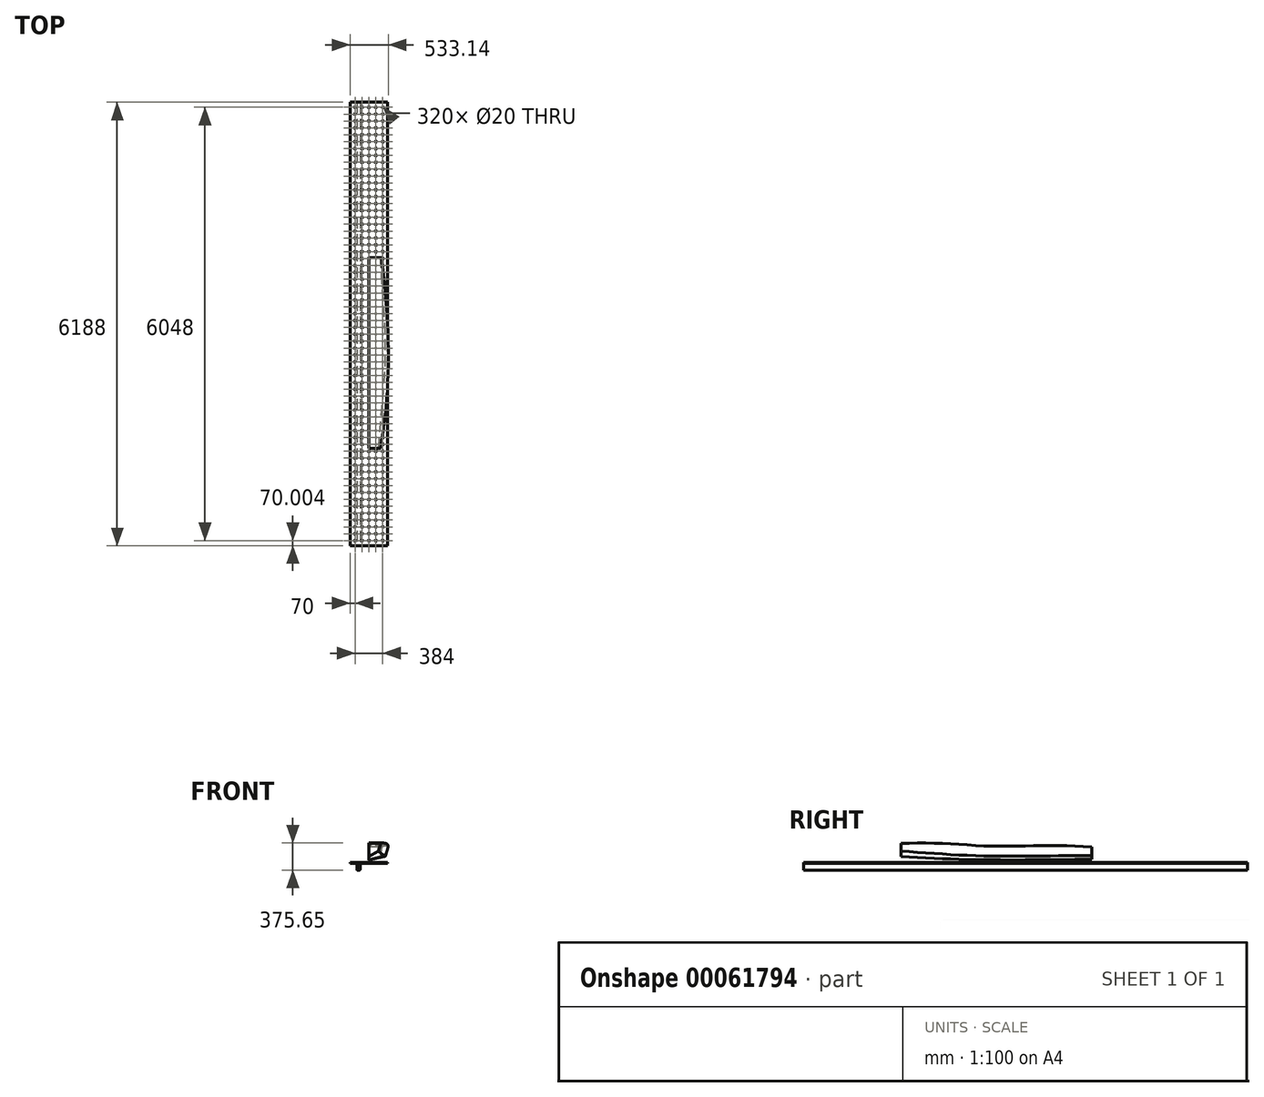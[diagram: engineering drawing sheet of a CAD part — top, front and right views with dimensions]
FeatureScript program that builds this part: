
annotation { "Feature Type Name" : "Feature", "Feature Type Description" : "" }
export const myFeature = defineFeature(function(context is Context, id is Id, definition is map)
    precondition{}
    {
        {
            var Q0;
            Q0=qCreatedBy(makeId("Right.planeOp"),FACE);
            var sketch = newSketch(context, id + "F0", { "sketchPlane" : qUnion([Q0])});
            skLineSegment(sketch, "E0.bottom", {"start": v(-75.52, -5.51) * mm, "end": v(6112.48, -5.51) * mm});
            skLineSegment(sketch, "E0.top", {"start": v(-75.52, 12.49) * mm, "end": v(6112.48, 12.49) * mm});
            skLineSegment(sketch, "E0.left", {"start": v(-75.52, -5.51) * mm, "end": v(-75.52, 12.49) * mm});
            skLineSegment(sketch, "E0.right", {"start": v(6112.48, -5.51) * mm, "end": v(6112.48, 12.49) * mm});
            skSolve(sketch);
        }
        {
            var Q0;
            Q0 = qSketchRegion(id + "F0", true);
            extrude(context, id + "F1", {"entities" : qUnion([Q0]), "endBound" : BoundingType.SYMMETRIC, "depth" : 524 * mm});
        }
        {
            var Q0;
            Q0=makeQuery(id+"F1.opExtrude","SWEPT_FACE",FACE,{"disambiguationData":[OSD([sQuery(id+"F0.wireOp",EDGE,"E0.top")])]});
            var sketch = newSketch(context, id + "F2", { "sketchPlane" : qUnion([Q0])});
            skCircle(sketch, "E1", {"center": v(0, -5.52) * mm, "radius": 10 * mm});
            skPoint(sketch, "E1.centerSnap0", {"position": v(0, -75.52) * mm});
            skCircle(sketch, "E2.0.1.0", {"center": v(0, 90.48) * mm, "radius": 10 * mm});
            skCircle(sketch, "E2.0.2.0", {"center": v(0, 186.48) * mm, "radius": 10 * mm});
            skCircle(sketch, "E2.0.3.0", {"center": v(0, 282.48) * mm, "radius": 10 * mm});
            skCircle(sketch, "E2.0.4.0", {"center": v(0, 378.48) * mm, "radius": 10 * mm});
            skCircle(sketch, "E2.0.5.0", {"center": v(0, 474.48) * mm, "radius": 10 * mm});
            skCircle(sketch, "E2.0.6.0", {"center": v(0, 570.48) * mm, "radius": 10 * mm});
            skCircle(sketch, "E2.0.7.0", {"center": v(0, 666.48) * mm, "radius": 10 * mm});
            skCircle(sketch, "E2.0.8.0", {"center": v(0, 762.48) * mm, "radius": 10 * mm});
            skCircle(sketch, "E2.0.9.0", {"center": v(0, 858.48) * mm, "radius": 10 * mm});
            skCircle(sketch, "E2.0.10.0", {"center": v(0, 954.48) * mm, "radius": 10 * mm});
            skCircle(sketch, "E2.0.11.0", {"center": v(0, 1050.48) * mm, "radius": 10 * mm});
            skCircle(sketch, "E2.0.12.0", {"center": v(0, 1146.48) * mm, "radius": 10 * mm});
            skCircle(sketch, "E2.0.13.0", {"center": v(0, 1242.48) * mm, "radius": 10 * mm});
            skCircle(sketch, "E2.0.14.0", {"center": v(0, 1338.48) * mm, "radius": 10 * mm});
            skCircle(sketch, "E2.0.15.0", {"center": v(0, 1434.48) * mm, "radius": 10 * mm});
            skCircle(sketch, "E2.0.16.0", {"center": v(0, 1530.48) * mm, "radius": 10 * mm});
            skCircle(sketch, "E2.0.17.0", {"center": v(0, 1626.48) * mm, "radius": 10 * mm});
            skCircle(sketch, "E2.0.18.0", {"center": v(0, 1722.48) * mm, "radius": 10 * mm});
            skCircle(sketch, "E2.0.19.0", {"center": v(0, 1818.48) * mm, "radius": 10 * mm});
            skCircle(sketch, "E2.0.20.0", {"center": v(0, 1914.48) * mm, "radius": 10 * mm});
            skCircle(sketch, "E2.0.21.0", {"center": v(0, 2010.48) * mm, "radius": 10 * mm});
            skCircle(sketch, "E2.0.22.0", {"center": v(0, 2106.48) * mm, "radius": 10 * mm});
            skCircle(sketch, "E2.0.23.0", {"center": v(0, 2202.48) * mm, "radius": 10 * mm});
            skCircle(sketch, "E2.0.24.0", {"center": v(0, 2298.48) * mm, "radius": 10 * mm});
            skCircle(sketch, "E2.0.25.0", {"center": v(0, 2394.48) * mm, "radius": 10 * mm});
            skCircle(sketch, "E2.0.26.0", {"center": v(0, 2490.48) * mm, "radius": 10 * mm});
            skCircle(sketch, "E2.0.27.0", {"center": v(0, 2586.48) * mm, "radius": 10 * mm});
            skCircle(sketch, "E2.0.28.0", {"center": v(0, 2682.48) * mm, "radius": 10 * mm});
            skCircle(sketch, "E2.0.29.0", {"center": v(0, 2778.48) * mm, "radius": 10 * mm});
            skCircle(sketch, "E2.0.30.0", {"center": v(0, 2874.48) * mm, "radius": 10 * mm});
            skCircle(sketch, "E2.0.31.0", {"center": v(0, 2970.48) * mm, "radius": 10 * mm});
            skCircle(sketch, "E2.0.32.0", {"center": v(0, 3066.48) * mm, "radius": 10 * mm});
            skCircle(sketch, "E2.0.33.0", {"center": v(0, 3162.48) * mm, "radius": 10 * mm});
            skCircle(sketch, "E2.0.34.0", {"center": v(0, 3258.48) * mm, "radius": 10 * mm});
            skCircle(sketch, "E2.0.35.0", {"center": v(0, 3354.48) * mm, "radius": 10 * mm});
            skCircle(sketch, "E2.0.36.0", {"center": v(0, 3450.48) * mm, "radius": 10 * mm});
            skCircle(sketch, "E2.0.37.0", {"center": v(0, 3546.48) * mm, "radius": 10 * mm});
            skCircle(sketch, "E2.0.38.0", {"center": v(0, 3642.48) * mm, "radius": 10 * mm});
            skCircle(sketch, "E2.0.39.0", {"center": v(0, 3738.48) * mm, "radius": 10 * mm});
            skCircle(sketch, "E2.0.40.0", {"center": v(0, 3834.48) * mm, "radius": 10 * mm});
            skCircle(sketch, "E2.0.41.0", {"center": v(0, 3930.48) * mm, "radius": 10 * mm});
            skCircle(sketch, "E2.0.42.0", {"center": v(0, 4026.48) * mm, "radius": 10 * mm});
            skCircle(sketch, "E2.0.43.0", {"center": v(0, 4122.48) * mm, "radius": 10 * mm});
            skCircle(sketch, "E2.0.44.0", {"center": v(0, 4218.48) * mm, "radius": 10 * mm});
            skCircle(sketch, "E2.0.45.0", {"center": v(0, 4314.48) * mm, "radius": 10 * mm});
            skCircle(sketch, "E2.0.46.0", {"center": v(0, 4410.48) * mm, "radius": 10 * mm});
            skCircle(sketch, "E2.0.47.0", {"center": v(0, 4506.48) * mm, "radius": 10 * mm});
            skCircle(sketch, "E2.0.48.0", {"center": v(0, 4602.48) * mm, "radius": 10 * mm});
            skCircle(sketch, "E2.0.49.0", {"center": v(0, 4698.48) * mm, "radius": 10 * mm});
            skCircle(sketch, "E2.1.0.0", {"center": v(96, -5.52) * mm, "radius": 10 * mm});
            skCircle(sketch, "E2.1.1.0", {"center": v(96, 90.48) * mm, "radius": 10 * mm});
            skCircle(sketch, "E2.1.2.0", {"center": v(96, 186.48) * mm, "radius": 10 * mm});
            skCircle(sketch, "E2.1.3.0", {"center": v(96, 282.48) * mm, "radius": 10 * mm});
            skCircle(sketch, "E2.1.4.0", {"center": v(96, 378.48) * mm, "radius": 10 * mm});
            skCircle(sketch, "E2.1.5.0", {"center": v(96, 474.48) * mm, "radius": 10 * mm});
            skCircle(sketch, "E2.1.6.0", {"center": v(96, 570.48) * mm, "radius": 10 * mm});
            skCircle(sketch, "E2.1.7.0", {"center": v(96, 666.48) * mm, "radius": 10 * mm});
            skCircle(sketch, "E2.1.8.0", {"center": v(96, 762.48) * mm, "radius": 10 * mm});
            skCircle(sketch, "E2.1.9.0", {"center": v(96, 858.48) * mm, "radius": 10 * mm});
            skCircle(sketch, "E2.1.10.0", {"center": v(96, 954.48) * mm, "radius": 10 * mm});
            skCircle(sketch, "E2.1.11.0", {"center": v(96, 1050.48) * mm, "radius": 10 * mm});
            skCircle(sketch, "E2.1.12.0", {"center": v(96, 1146.48) * mm, "radius": 10 * mm});
            skCircle(sketch, "E2.1.13.0", {"center": v(96, 1242.48) * mm, "radius": 10 * mm});
            skCircle(sketch, "E2.1.14.0", {"center": v(96, 1338.48) * mm, "radius": 10 * mm});
            skCircle(sketch, "E2.1.15.0", {"center": v(96, 1434.48) * mm, "radius": 10 * mm});
            skCircle(sketch, "E2.1.16.0", {"center": v(96, 1530.48) * mm, "radius": 10 * mm});
            skCircle(sketch, "E2.1.17.0", {"center": v(96, 1626.48) * mm, "radius": 10 * mm});
            skCircle(sketch, "E2.1.18.0", {"center": v(96, 1722.48) * mm, "radius": 10 * mm});
            skCircle(sketch, "E2.1.19.0", {"center": v(96, 1818.48) * mm, "radius": 10 * mm});
            skCircle(sketch, "E2.1.20.0", {"center": v(96, 1914.48) * mm, "radius": 10 * mm});
            skCircle(sketch, "E2.1.21.0", {"center": v(96, 2010.48) * mm, "radius": 10 * mm});
            skCircle(sketch, "E2.1.22.0", {"center": v(96, 2106.48) * mm, "radius": 10 * mm});
            skCircle(sketch, "E2.1.23.0", {"center": v(96, 2202.48) * mm, "radius": 10 * mm});
            skCircle(sketch, "E2.1.24.0", {"center": v(96, 2298.48) * mm, "radius": 10 * mm});
            skCircle(sketch, "E2.1.25.0", {"center": v(96, 2394.48) * mm, "radius": 10 * mm});
            skCircle(sketch, "E2.1.26.0", {"center": v(96, 2490.48) * mm, "radius": 10 * mm});
            skCircle(sketch, "E2.1.27.0", {"center": v(96, 2586.48) * mm, "radius": 10 * mm});
            skCircle(sketch, "E2.1.28.0", {"center": v(96, 2682.48) * mm, "radius": 10 * mm});
            skCircle(sketch, "E2.1.29.0", {"center": v(96, 2778.48) * mm, "radius": 10 * mm});
            skCircle(sketch, "E2.1.30.0", {"center": v(96, 2874.48) * mm, "radius": 10 * mm});
            skCircle(sketch, "E2.1.31.0", {"center": v(96, 2970.48) * mm, "radius": 10 * mm});
            skCircle(sketch, "E2.1.32.0", {"center": v(96, 3066.48) * mm, "radius": 10 * mm});
            skCircle(sketch, "E2.1.33.0", {"center": v(96, 3162.48) * mm, "radius": 10 * mm});
            skCircle(sketch, "E2.1.34.0", {"center": v(96, 3258.48) * mm, "radius": 10 * mm});
            skCircle(sketch, "E2.1.35.0", {"center": v(96, 3354.48) * mm, "radius": 10 * mm});
            skCircle(sketch, "E2.1.36.0", {"center": v(96, 3450.48) * mm, "radius": 10 * mm});
            skCircle(sketch, "E2.1.37.0", {"center": v(96, 3546.48) * mm, "radius": 10 * mm});
            skCircle(sketch, "E2.1.38.0", {"center": v(96, 3642.48) * mm, "radius": 10 * mm});
            skCircle(sketch, "E2.1.39.0", {"center": v(96, 3738.48) * mm, "radius": 10 * mm});
            skCircle(sketch, "E2.1.40.0", {"center": v(96, 3834.48) * mm, "radius": 10 * mm});
            skCircle(sketch, "E2.1.41.0", {"center": v(96, 3930.48) * mm, "radius": 10 * mm});
            skCircle(sketch, "E2.1.42.0", {"center": v(96, 4026.48) * mm, "radius": 10 * mm});
            skCircle(sketch, "E2.1.43.0", {"center": v(96, 4122.48) * mm, "radius": 10 * mm});
            skCircle(sketch, "E2.1.44.0", {"center": v(96, 4218.48) * mm, "radius": 10 * mm});
            skCircle(sketch, "E2.1.45.0", {"center": v(96, 4314.48) * mm, "radius": 10 * mm});
            skCircle(sketch, "E2.1.46.0", {"center": v(96, 4410.48) * mm, "radius": 10 * mm});
            skCircle(sketch, "E2.1.47.0", {"center": v(96, 4506.48) * mm, "radius": 10 * mm});
            skCircle(sketch, "E2.1.48.0", {"center": v(96, 4602.48) * mm, "radius": 10 * mm});
            skCircle(sketch, "E2.1.49.0", {"center": v(96, 4698.48) * mm, "radius": 10 * mm});
            skCircle(sketch, "E2.2.0.0", {"center": v(192, -5.52) * mm, "radius": 10 * mm});
            skCircle(sketch, "E2.2.1.0", {"center": v(192, 90.48) * mm, "radius": 10 * mm});
            skCircle(sketch, "E2.2.2.0", {"center": v(192, 186.48) * mm, "radius": 10 * mm});
            skCircle(sketch, "E2.2.3.0", {"center": v(192, 282.48) * mm, "radius": 10 * mm});
            skCircle(sketch, "E2.2.4.0", {"center": v(192, 378.48) * mm, "radius": 10 * mm});
            skCircle(sketch, "E2.2.5.0", {"center": v(192, 474.48) * mm, "radius": 10 * mm});
            skCircle(sketch, "E2.2.6.0", {"center": v(192, 570.48) * mm, "radius": 10 * mm});
            skCircle(sketch, "E2.2.7.0", {"center": v(192, 666.48) * mm, "radius": 10 * mm});
            skCircle(sketch, "E2.2.8.0", {"center": v(192, 762.48) * mm, "radius": 10 * mm});
            skCircle(sketch, "E2.2.9.0", {"center": v(192, 858.48) * mm, "radius": 10 * mm});
            skCircle(sketch, "E2.2.10.0", {"center": v(192, 954.48) * mm, "radius": 10 * mm});
            skCircle(sketch, "E2.2.11.0", {"center": v(192, 1050.48) * mm, "radius": 10 * mm});
            skCircle(sketch, "E2.2.12.0", {"center": v(192, 1146.48) * mm, "radius": 10 * mm});
            skCircle(sketch, "E2.2.13.0", {"center": v(192, 1242.48) * mm, "radius": 10 * mm});
            skCircle(sketch, "E2.2.14.0", {"center": v(192, 1338.48) * mm, "radius": 10 * mm});
            skCircle(sketch, "E2.2.15.0", {"center": v(192, 1434.48) * mm, "radius": 10 * mm});
            skCircle(sketch, "E2.2.16.0", {"center": v(192, 1530.48) * mm, "radius": 10 * mm});
            skCircle(sketch, "E2.2.17.0", {"center": v(192, 1626.48) * mm, "radius": 10 * mm});
            skCircle(sketch, "E2.2.18.0", {"center": v(192, 1722.48) * mm, "radius": 10 * mm});
            skCircle(sketch, "E2.2.19.0", {"center": v(192, 1818.48) * mm, "radius": 10 * mm});
            skCircle(sketch, "E2.2.20.0", {"center": v(192, 1914.48) * mm, "radius": 10 * mm});
            skCircle(sketch, "E2.2.21.0", {"center": v(192, 2010.48) * mm, "radius": 10 * mm});
            skCircle(sketch, "E2.2.22.0", {"center": v(192, 2106.48) * mm, "radius": 10 * mm});
            skCircle(sketch, "E2.2.23.0", {"center": v(192, 2202.48) * mm, "radius": 10 * mm});
            skCircle(sketch, "E2.2.24.0", {"center": v(192, 2298.48) * mm, "radius": 10 * mm});
            skCircle(sketch, "E2.2.25.0", {"center": v(192, 2394.48) * mm, "radius": 10 * mm});
            skCircle(sketch, "E2.2.26.0", {"center": v(192, 2490.48) * mm, "radius": 10 * mm});
            skCircle(sketch, "E2.2.27.0", {"center": v(192, 2586.48) * mm, "radius": 10 * mm});
            skCircle(sketch, "E2.2.28.0", {"center": v(192, 2682.48) * mm, "radius": 10 * mm});
            skCircle(sketch, "E2.2.29.0", {"center": v(192, 2778.48) * mm, "radius": 10 * mm});
            skCircle(sketch, "E2.2.30.0", {"center": v(192, 2874.48) * mm, "radius": 10 * mm});
            skCircle(sketch, "E2.2.31.0", {"center": v(192, 2970.48) * mm, "radius": 10 * mm});
            skCircle(sketch, "E2.2.32.0", {"center": v(192, 3066.48) * mm, "radius": 10 * mm});
            skCircle(sketch, "E2.2.33.0", {"center": v(192, 3162.48) * mm, "radius": 10 * mm});
            skCircle(sketch, "E2.2.34.0", {"center": v(192, 3258.48) * mm, "radius": 10 * mm});
            skCircle(sketch, "E2.2.35.0", {"center": v(192, 3354.48) * mm, "radius": 10 * mm});
            skCircle(sketch, "E2.2.36.0", {"center": v(192, 3450.48) * mm, "radius": 10 * mm});
            skCircle(sketch, "E2.2.37.0", {"center": v(192, 3546.48) * mm, "radius": 10 * mm});
            skCircle(sketch, "E2.2.38.0", {"center": v(192, 3642.48) * mm, "radius": 10 * mm});
            skCircle(sketch, "E2.2.39.0", {"center": v(192, 3738.48) * mm, "radius": 10 * mm});
            skCircle(sketch, "E2.2.40.0", {"center": v(192, 3834.48) * mm, "radius": 10 * mm});
            skCircle(sketch, "E2.2.41.0", {"center": v(192, 3930.48) * mm, "radius": 10 * mm});
            skCircle(sketch, "E2.2.42.0", {"center": v(192, 4026.48) * mm, "radius": 10 * mm});
            skCircle(sketch, "E2.2.43.0", {"center": v(192, 4122.48) * mm, "radius": 10 * mm});
            skCircle(sketch, "E2.2.44.0", {"center": v(192, 4218.48) * mm, "radius": 10 * mm});
            skCircle(sketch, "E2.2.45.0", {"center": v(192, 4314.48) * mm, "radius": 10 * mm});
            skCircle(sketch, "E2.2.46.0", {"center": v(192, 4410.48) * mm, "radius": 10 * mm});
            skCircle(sketch, "E2.2.47.0", {"center": v(192, 4506.48) * mm, "radius": 10 * mm});
            skCircle(sketch, "E2.2.48.0", {"center": v(192, 4602.48) * mm, "radius": 10 * mm});
            skCircle(sketch, "E2.2.49.0", {"center": v(192, 4698.48) * mm, "radius": 10 * mm});
            skLineSegment(sketch, "E2.direction1", {"start": v(0, -5.52) * mm, "end": v(96, -5.52) * mm, "construction": true});
            skLineSegment(sketch, "E2.direction2", {"start": v(0, -5.52) * mm, "end": v(0, 90.48) * mm, "construction": true});
            skCircle(sketch, "E3.0.0.50", {"center": v(0, 4794.48) * mm, "radius": 10 * mm});
            skCircle(sketch, "E3.0.0.51", {"center": v(0, 4890.48) * mm, "radius": 10 * mm});
            skCircle(sketch, "E3.0.0.52", {"center": v(0, 4986.48) * mm, "radius": 10 * mm});
            skCircle(sketch, "E3.0.0.53", {"center": v(0, 5082.48) * mm, "radius": 10 * mm});
            skCircle(sketch, "E3.0.0.54", {"center": v(0, 5178.48) * mm, "radius": 10 * mm});
            skCircle(sketch, "E3.0.0.55", {"center": v(0, 5274.48) * mm, "radius": 10 * mm});
            skCircle(sketch, "E3.0.0.56", {"center": v(0, 5370.48) * mm, "radius": 10 * mm});
            skCircle(sketch, "E3.0.0.57", {"center": v(0, 5466.48) * mm, "radius": 10 * mm});
            skCircle(sketch, "E3.0.0.58", {"center": v(0, 5562.48) * mm, "radius": 10 * mm});
            skCircle(sketch, "E3.0.0.59", {"center": v(0, 5658.48) * mm, "radius": 10 * mm});
            skCircle(sketch, "E3.0.0.60", {"center": v(0, 5754.48) * mm, "radius": 10 * mm});
            skCircle(sketch, "E3.0.0.61", {"center": v(0, 5850.48) * mm, "radius": 10 * mm});
            skCircle(sketch, "E3.0.0.62", {"center": v(0, 5946.48) * mm, "radius": 10 * mm});
            skCircle(sketch, "E3.0.0.63", {"center": v(0, 6042.48) * mm, "radius": 10 * mm});
            skCircle(sketch, "E3.0.1.50", {"center": v(96, 4794.48) * mm, "radius": 10 * mm});
            skCircle(sketch, "E3.0.1.51", {"center": v(96, 4890.48) * mm, "radius": 10 * mm});
            skCircle(sketch, "E3.0.1.52", {"center": v(96, 4986.48) * mm, "radius": 10 * mm});
            skCircle(sketch, "E3.0.1.53", {"center": v(96, 5082.48) * mm, "radius": 10 * mm});
            skCircle(sketch, "E3.0.1.54", {"center": v(96, 5178.48) * mm, "radius": 10 * mm});
            skCircle(sketch, "E3.0.1.55", {"center": v(96, 5274.48) * mm, "radius": 10 * mm});
            skCircle(sketch, "E3.0.1.56", {"center": v(96, 5370.48) * mm, "radius": 10 * mm});
            skCircle(sketch, "E3.0.1.57", {"center": v(96, 5466.48) * mm, "radius": 10 * mm});
            skCircle(sketch, "E3.0.1.58", {"center": v(96, 5562.48) * mm, "radius": 10 * mm});
            skCircle(sketch, "E3.0.1.59", {"center": v(96, 5658.48) * mm, "radius": 10 * mm});
            skCircle(sketch, "E3.0.1.60", {"center": v(96, 5754.48) * mm, "radius": 10 * mm});
            skCircle(sketch, "E3.0.1.61", {"center": v(96, 5850.48) * mm, "radius": 10 * mm});
            skCircle(sketch, "E3.0.1.62", {"center": v(96, 5946.48) * mm, "radius": 10 * mm});
            skCircle(sketch, "E3.0.1.63", {"center": v(96, 6042.48) * mm, "radius": 10 * mm});
            skCircle(sketch, "E3.0.2.50", {"center": v(192, 4794.48) * mm, "radius": 10 * mm});
            skCircle(sketch, "E3.0.2.51", {"center": v(192, 4890.48) * mm, "radius": 10 * mm});
            skCircle(sketch, "E3.0.2.52", {"center": v(192, 4986.48) * mm, "radius": 10 * mm});
            skCircle(sketch, "E3.0.2.53", {"center": v(192, 5082.48) * mm, "radius": 10 * mm});
            skCircle(sketch, "E3.0.2.54", {"center": v(192, 5178.48) * mm, "radius": 10 * mm});
            skCircle(sketch, "E3.0.2.55", {"center": v(192, 5274.48) * mm, "radius": 10 * mm});
            skCircle(sketch, "E3.0.2.56", {"center": v(192, 5370.48) * mm, "radius": 10 * mm});
            skCircle(sketch, "E3.0.2.57", {"center": v(192, 5466.48) * mm, "radius": 10 * mm});
            skCircle(sketch, "E3.0.2.58", {"center": v(192, 5562.48) * mm, "radius": 10 * mm});
            skCircle(sketch, "E3.0.2.59", {"center": v(192, 5658.48) * mm, "radius": 10 * mm});
            skCircle(sketch, "E3.0.2.60", {"center": v(192, 5754.48) * mm, "radius": 10 * mm});
            skCircle(sketch, "E3.0.2.61", {"center": v(192, 5850.48) * mm, "radius": 10 * mm});
            skCircle(sketch, "E3.0.2.62", {"center": v(192, 5946.48) * mm, "radius": 10 * mm});
            skCircle(sketch, "E3.0.2.63", {"center": v(192, 6042.48) * mm, "radius": 10 * mm});
            skCircle(sketch, "E4.MirrorC", {"center": v(-96, 186.48) * mm, "radius": 10 * mm});
            skCircle(sketch, "E5.MirrorC", {"center": v(-96, -5.52) * mm, "radius": 10 * mm});
            skCircle(sketch, "E6.MirrorC", {"center": v(-96, 90.48) * mm, "radius": 10 * mm});
            skCircle(sketch, "E7.MirrorC", {"center": v(-192, 90.48) * mm, "radius": 10 * mm});
            skCircle(sketch, "E8.MirrorC", {"center": v(-192, 282.48) * mm, "radius": 10 * mm});
            skCircle(sketch, "E9.MirrorC", {"center": v(-96, 282.48) * mm, "radius": 10 * mm});
            skLineSegment(sketch, "E10.MirrorCS", {"start": v(0, -5.52) * mm, "end": v(-96, -5.52) * mm, "construction": true});
            skCircle(sketch, "E11.MirrorC", {"center": v(-192, 186.48) * mm, "radius": 10 * mm});
            skCircle(sketch, "E12.MirrorC", {"center": v(-192, -5.52) * mm, "radius": 10 * mm});
            skCircle(sketch, "E13.MirrorC", {"center": v(-96, 1338.48) * mm, "radius": 10 * mm});
            skCircle(sketch, "E14.MirrorC", {"center": v(-192, 954.48) * mm, "radius": 10 * mm});
            skCircle(sketch, "E15.MirrorC", {"center": v(-96, 1146.48) * mm, "radius": 10 * mm});
            skCircle(sketch, "E16.MirrorC", {"center": v(-192, 762.48) * mm, "radius": 10 * mm});
            skCircle(sketch, "E17.MirrorC", {"center": v(-96, 954.48) * mm, "radius": 10 * mm});
            skCircle(sketch, "E18.MirrorC", {"center": v(-192, 570.48) * mm, "radius": 10 * mm});
            skCircle(sketch, "E19.MirrorC", {"center": v(-96, 762.48) * mm, "radius": 10 * mm});
            skCircle(sketch, "E20.MirrorC", {"center": v(-192, 858.48) * mm, "radius": 10 * mm});
            skCircle(sketch, "E21.MirrorC", {"center": v(-192, 474.48) * mm, "radius": 10 * mm});
            skCircle(sketch, "E22.MirrorC", {"center": v(-96, 1050.48) * mm, "radius": 10 * mm});
            skCircle(sketch, "E23.MirrorC", {"center": v(-192, 666.48) * mm, "radius": 10 * mm});
            skCircle(sketch, "E24.MirrorC", {"center": v(-96, 858.48) * mm, "radius": 10 * mm});
            skCircle(sketch, "E25.MirrorC", {"center": v(-192, 1626.48) * mm, "radius": 10 * mm});
            skCircle(sketch, "E26.MirrorC", {"center": v(-192, 1434.48) * mm, "radius": 10 * mm});
            skCircle(sketch, "E27.MirrorC", {"center": v(-192, 1530.48) * mm, "radius": 10 * mm});
            skCircle(sketch, "E28.MirrorC", {"center": v(-192, 1338.48) * mm, "radius": 10 * mm});
            skCircle(sketch, "E29.MirrorC", {"center": v(-96, 1242.48) * mm, "radius": 10 * mm});
            skCircle(sketch, "E30.MirrorC", {"center": v(-192, 1050.48) * mm, "radius": 10 * mm});
            skCircle(sketch, "E31.MirrorC", {"center": v(-192, 1146.48) * mm, "radius": 10 * mm});
            skCircle(sketch, "E32.MirrorC", {"center": v(-96, 1434.48) * mm, "radius": 10 * mm});
            skCircle(sketch, "E33.MirrorC", {"center": v(-192, 1242.48) * mm, "radius": 10 * mm});
            skCircle(sketch, "E34.MirrorC", {"center": v(-96, 1530.48) * mm, "radius": 10 * mm});
            skCircle(sketch, "E35.MirrorC", {"center": v(-96, 378.48) * mm, "radius": 10 * mm});
            skCircle(sketch, "E36.MirrorC", {"center": v(-96, 474.48) * mm, "radius": 10 * mm});
            skCircle(sketch, "E37.MirrorC", {"center": v(-96, 1626.48) * mm, "radius": 10 * mm});
            skCircle(sketch, "E38.MirrorC", {"center": v(-96, 666.48) * mm, "radius": 10 * mm});
            skCircle(sketch, "E39.MirrorC", {"center": v(-96, 570.48) * mm, "radius": 10 * mm});
            skCircle(sketch, "E40.MirrorC", {"center": v(-192, 378.48) * mm, "radius": 10 * mm});
            skCircle(sketch, "E41.MirrorC", {"center": v(-192, 2010.48) * mm, "radius": 10 * mm});
            skCircle(sketch, "E42.MirrorC", {"center": v(-96, 1722.48) * mm, "radius": 10 * mm});
            skCircle(sketch, "E43.MirrorC", {"center": v(-192, 1722.48) * mm, "radius": 10 * mm});
            skCircle(sketch, "E44.MirrorC", {"center": v(-192, 1818.48) * mm, "radius": 10 * mm});
            skCircle(sketch, "E45.MirrorC", {"center": v(-192, 1914.48) * mm, "radius": 10 * mm});
            skCircle(sketch, "E46.MirrorC", {"center": v(-96, 1818.48) * mm, "radius": 10 * mm});
            skCircle(sketch, "E47.MirrorC", {"center": v(-96, 2010.48) * mm, "radius": 10 * mm});
            skCircle(sketch, "E48.MirrorC", {"center": v(-96, 1914.48) * mm, "radius": 10 * mm});
            skCircle(sketch, "E49.MirrorC", {"center": v(-192, 2682.48) * mm, "radius": 10 * mm});
            skCircle(sketch, "E50.MirrorC", {"center": v(-192, 2586.48) * mm, "radius": 10 * mm});
            skCircle(sketch, "E51.MirrorC", {"center": v(-96, 2778.48) * mm, "radius": 10 * mm});
            skCircle(sketch, "E52.MirrorC", {"center": v(-96, 2298.48) * mm, "radius": 10 * mm});
            skCircle(sketch, "E53.MirrorC", {"center": v(-192, 2490.48) * mm, "radius": 10 * mm});
            skCircle(sketch, "E54.MirrorC", {"center": v(-96, 2682.48) * mm, "radius": 10 * mm});
            skCircle(sketch, "E55.MirrorC", {"center": v(-192, 2106.48) * mm, "radius": 10 * mm});
            skCircle(sketch, "E56.MirrorC", {"center": v(-96, 2106.48) * mm, "radius": 10 * mm});
            skCircle(sketch, "E57.MirrorC", {"center": v(-192, 2298.48) * mm, "radius": 10 * mm});
            skCircle(sketch, "E58.MirrorC", {"center": v(-96, 2490.48) * mm, "radius": 10 * mm});
            skCircle(sketch, "E59.MirrorC", {"center": v(-192, 2394.48) * mm, "radius": 10 * mm});
            skCircle(sketch, "E60.MirrorC", {"center": v(-96, 2394.48) * mm, "radius": 10 * mm});
            skCircle(sketch, "E61.MirrorC", {"center": v(-192, 2778.48) * mm, "radius": 10 * mm});
            skCircle(sketch, "E62.MirrorC", {"center": v(-96, 2202.48) * mm, "radius": 10 * mm});
            skCircle(sketch, "E63.MirrorC", {"center": v(-192, 2202.48) * mm, "radius": 10 * mm});
            skCircle(sketch, "E64.MirrorC", {"center": v(-96, 2586.48) * mm, "radius": 10 * mm});
            skCircle(sketch, "E65.MirrorC", {"center": v(-96, 2970.48) * mm, "radius": 10 * mm});
            skCircle(sketch, "E66.MirrorC", {"center": v(-96, 3066.48) * mm, "radius": 10 * mm});
            skCircle(sketch, "E67.MirrorC", {"center": v(-192, 4122.48) * mm, "radius": 10 * mm});
            skCircle(sketch, "E68.MirrorC", {"center": v(-96, 3738.48) * mm, "radius": 10 * mm});
            skCircle(sketch, "E69.MirrorC", {"center": v(-96, 2874.48) * mm, "radius": 10 * mm});
            skCircle(sketch, "E70.MirrorC", {"center": v(-192, 3066.48) * mm, "radius": 10 * mm});
            skCircle(sketch, "E71.MirrorC", {"center": v(-96, 3258.48) * mm, "radius": 10 * mm});
            skCircle(sketch, "E72.MirrorC", {"center": v(-192, 2874.48) * mm, "radius": 10 * mm});
            skCircle(sketch, "E73.MirrorC", {"center": v(-96, 3162.48) * mm, "radius": 10 * mm});
            skCircle(sketch, "E74.MirrorC", {"center": v(-96, 3930.48) * mm, "radius": 10 * mm});
            skCircle(sketch, "E75.MirrorC", {"center": v(-192, 3546.48) * mm, "radius": 10 * mm});
            skCircle(sketch, "E76.MirrorC", {"center": v(-192, 3738.48) * mm, "radius": 10 * mm});
            skCircle(sketch, "E77.MirrorC", {"center": v(-192, 3834.48) * mm, "radius": 10 * mm});
            skCircle(sketch, "E78.MirrorC", {"center": v(-96, 4026.48) * mm, "radius": 10 * mm});
            skCircle(sketch, "E79.MirrorC", {"center": v(-96, 3450.48) * mm, "radius": 10 * mm});
            skCircle(sketch, "E80.MirrorC", {"center": v(-96, 4122.48) * mm, "radius": 10 * mm});
            skCircle(sketch, "E81.MirrorC", {"center": v(-192, 3930.48) * mm, "radius": 10 * mm});
            skCircle(sketch, "E82.MirrorC", {"center": v(-192, 3162.48) * mm, "radius": 10 * mm});
            skCircle(sketch, "E83.MirrorC", {"center": v(-96, 3642.48) * mm, "radius": 10 * mm});
            skCircle(sketch, "E84.MirrorC", {"center": v(-192, 3450.48) * mm, "radius": 10 * mm});
            skCircle(sketch, "E85.MirrorC", {"center": v(-96, 3546.48) * mm, "radius": 10 * mm});
            skCircle(sketch, "E86.MirrorC", {"center": v(-192, 4026.48) * mm, "radius": 10 * mm});
            skCircle(sketch, "E87.MirrorC", {"center": v(-96, 3354.48) * mm, "radius": 10 * mm});
            skCircle(sketch, "E88.MirrorC", {"center": v(-192, 3354.48) * mm, "radius": 10 * mm});
            skCircle(sketch, "E89.MirrorC", {"center": v(-192, 2970.48) * mm, "radius": 10 * mm});
            skCircle(sketch, "E90.MirrorC", {"center": v(-192, 3258.48) * mm, "radius": 10 * mm});
            skCircle(sketch, "E91.MirrorC", {"center": v(-96, 3834.48) * mm, "radius": 10 * mm});
            skCircle(sketch, "E92.MirrorC", {"center": v(-192, 3642.48) * mm, "radius": 10 * mm});
            skCircle(sketch, "E93.MirrorC", {"center": v(-192, 5370.48) * mm, "radius": 10 * mm});
            skCircle(sketch, "E94.MirrorC", {"center": v(-96, 5754.48) * mm, "radius": 10 * mm});
            skCircle(sketch, "E95.MirrorC", {"center": v(-192, 4314.48) * mm, "radius": 10 * mm});
            skCircle(sketch, "E96.MirrorC", {"center": v(-96, 4986.48) * mm, "radius": 10 * mm});
            skCircle(sketch, "E97.MirrorC", {"center": v(-192, 5082.48) * mm, "radius": 10 * mm});
            skCircle(sketch, "E98.MirrorC", {"center": v(-192, 4506.48) * mm, "radius": 10 * mm});
            skCircle(sketch, "E99.MirrorC", {"center": v(-96, 5658.48) * mm, "radius": 10 * mm});
            skCircle(sketch, "E100.MirrorC", {"center": v(-192, 5754.48) * mm, "radius": 10 * mm});
            skCircle(sketch, "E101.MirrorC", {"center": v(-192, 4218.48) * mm, "radius": 10 * mm});
            skCircle(sketch, "E102.MirrorC", {"center": v(-96, 4410.48) * mm, "radius": 10 * mm});
            skCircle(sketch, "E103.MirrorC", {"center": v(-96, 5562.48) * mm, "radius": 10 * mm});
            skCircle(sketch, "E104.MirrorC", {"center": v(-192, 5658.48) * mm, "radius": 10 * mm});
            skCircle(sketch, "E105.MirrorC", {"center": v(-96, 5178.48) * mm, "radius": 10 * mm});
            skCircle(sketch, "E106.MirrorC", {"center": v(-192, 4698.48) * mm, "radius": 10 * mm});
            skCircle(sketch, "E107.MirrorC", {"center": v(-192, 5274.48) * mm, "radius": 10 * mm});
            skCircle(sketch, "E108.MirrorC", {"center": v(-192, 4602.48) * mm, "radius": 10 * mm});
            skCircle(sketch, "E109.MirrorC", {"center": v(-96, 4794.48) * mm, "radius": 10 * mm});
            skCircle(sketch, "E110.MirrorC", {"center": v(-96, 4314.48) * mm, "radius": 10 * mm});
            skCircle(sketch, "E111.MirrorC", {"center": v(-96, 4602.48) * mm, "radius": 10 * mm});
            skCircle(sketch, "E112.MirrorC", {"center": v(-96, 4506.48) * mm, "radius": 10 * mm});
            skCircle(sketch, "E113.MirrorC", {"center": v(-96, 5274.48) * mm, "radius": 10 * mm});
            skCircle(sketch, "E114.MirrorC", {"center": v(-192, 4410.48) * mm, "radius": 10 * mm});
            skCircle(sketch, "E115.MirrorC", {"center": v(-96, 5466.48) * mm, "radius": 10 * mm});
            skCircle(sketch, "E116.MirrorC", {"center": v(-192, 4986.48) * mm, "radius": 10 * mm});
            skCircle(sketch, "E117.MirrorC", {"center": v(-192, 4794.48) * mm, "radius": 10 * mm});
            skCircle(sketch, "E118.MirrorC", {"center": v(-192, 5178.48) * mm, "radius": 10 * mm});
            skCircle(sketch, "E119.MirrorC", {"center": v(-192, 5466.48) * mm, "radius": 10 * mm});
            skCircle(sketch, "E120.MirrorC", {"center": v(-96, 4698.48) * mm, "radius": 10 * mm});
            skCircle(sketch, "E121.MirrorC", {"center": v(-96, 5370.48) * mm, "radius": 10 * mm});
            skCircle(sketch, "E122.MirrorC", {"center": v(-96, 5082.48) * mm, "radius": 10 * mm});
            skCircle(sketch, "E123.MirrorC", {"center": v(-96, 4890.48) * mm, "radius": 10 * mm});
            skCircle(sketch, "E124.MirrorC", {"center": v(-192, 4890.48) * mm, "radius": 10 * mm});
            skCircle(sketch, "E125.MirrorC", {"center": v(-96, 4218.48) * mm, "radius": 10 * mm});
            skCircle(sketch, "E126.MirrorC", {"center": v(-192, 5562.48) * mm, "radius": 10 * mm});
            skCircle(sketch, "E127.MirrorC", {"center": v(-192, 5850.48) * mm, "radius": 10 * mm});
            skCircle(sketch, "E128.MirrorC", {"center": v(-192, 6042.48) * mm, "radius": 10 * mm});
            skCircle(sketch, "E129.MirrorC", {"center": v(-96, 5946.48) * mm, "radius": 10 * mm});
            skCircle(sketch, "E130.MirrorC", {"center": v(-96, 5850.48) * mm, "radius": 10 * mm});
            skCircle(sketch, "E131.MirrorC", {"center": v(-192, 5946.48) * mm, "radius": 10 * mm});
            skCircle(sketch, "E132.MirrorC", {"center": v(-96, 6042.48) * mm, "radius": 10 * mm});
            skLineSegment(sketch, "E133", {"start": v(0, -75.52) * mm, "end": v(0, 6112.48) * mm, "construction": true});
            skLineSegment(sketch, "E134", {"start": v(-192, -5.52) * mm, "end": v(192, -5.52) * mm, "construction": true});
            skLineSegment(sketch, "E135", {"start": v(-192, 282.48) * mm, "end": v(192, 282.48) * mm, "construction": true});
            skLineSegment(sketch, "E136", {"start": v(-192, 570.48) * mm, "end": v(192, 570.48) * mm, "construction": true});
            skLineSegment(sketch, "E137", {"start": v(-192, 858.48) * mm, "end": v(192, 858.48) * mm, "construction": true});
            skLineSegment(sketch, "E138", {"start": v(-192, 1434.48) * mm, "end": v(192, 1434.48) * mm, "construction": true});
            skLineSegment(sketch, "E139", {"start": v(-192, 1722.48) * mm, "end": v(192, 1722.48) * mm, "construction": true});
            skLineSegment(sketch, "E140", {"start": v(-192, 1146.48) * mm, "end": v(192, 1146.48) * mm, "construction": true});
            skLineSegment(sketch, "E141", {"start": v(-192, 2010.48) * mm, "end": v(192, 2010.48) * mm, "construction": true});
            skLineSegment(sketch, "E142", {"start": v(-192, 2298.48) * mm, "end": v(192, 2298.48) * mm, "construction": true});
            skLineSegment(sketch, "E143", {"start": v(-192, 2586.48) * mm, "end": v(192, 2586.48) * mm, "construction": true});
            skLineSegment(sketch, "E144", {"start": v(-192, 2874.48) * mm, "end": v(192, 2874.48) * mm, "construction": true});
            skLineSegment(sketch, "E145", {"start": v(-192, 3162.48) * mm, "end": v(192, 3162.48) * mm, "construction": true});
            skLineSegment(sketch, "E146", {"start": v(-192, 3450.48) * mm, "end": v(192, 3450.48) * mm});
            skLineSegment(sketch, "E147", {"start": v(-192, 3738.48) * mm, "end": v(192, 3738.48) * mm, "construction": true});
            skLineSegment(sketch, "E148", {"start": v(-192, 4026.48) * mm, "end": v(192, 4026.48) * mm, "construction": true});
            skLineSegment(sketch, "E149", {"start": v(-192, 4314.48) * mm, "end": v(192, 4314.48) * mm, "construction": true});
            skLineSegment(sketch, "E150", {"start": v(-192, 4602.48) * mm, "end": v(192, 4602.48) * mm, "construction": true});
            skLineSegment(sketch, "E151", {"start": v(-192, 4890.48) * mm, "end": v(192, 4890.48) * mm, "construction": true});
            skLineSegment(sketch, "E152", {"start": v(-192, 5178.48) * mm, "end": v(192, 5178.48) * mm, "construction": true});
            skLineSegment(sketch, "E153", {"start": v(-192, 5466.48) * mm, "end": v(192, 5466.48) * mm, "construction": true});
            skLineSegment(sketch, "E154", {"start": v(-192, 5754.48) * mm, "end": v(192, 5754.48) * mm, "construction": true});
            skLineSegment(sketch, "E155", {"start": v(-192, 6042.48) * mm, "end": v(192, 6042.48) * mm, "construction": true});
            skSolve(sketch);
        }
        {
            var Q0;
            Q0 = qSketchRegion(id + "F2", true);
            extrude(context, id + "F3", {"entities" : qUnion([Q0]), "operationType" : NewBodyOperationType.REMOVE, "oppositeDirection" : true, "depth" : 25 * mm});
        }
        {
            var Q0;
            Q0=makeQuery(id+"F1.opExtrude","SWEPT_FACE",FACE,{"disambiguationData":[OSD([sQuery(id+"F0.wireOp",EDGE,"E0.left")])]});
            cPlane(context, id + "F4", {"entities" : qUnion([Q0]), "cplaneType" : CPlaneType.OFFSET, "offset" : 3216 * mm, "oppositeDirection" : true, "width" : 150 * mm, "height" : 150 * mm});
        }
        {
            var Q0;
            Q0=makeQuery(id+"F1.opExtrude","SWEPT_FACE",FACE,{"disambiguationData":[OSD([sQuery(id+"F0.wireOp",EDGE,"E0.left")])]});
            var sketch = newSketch(context, id + "F5", { "sketchPlane" : qUnion([Q0])});
            skLineSegment(sketch, "E156.0", {"start": v(-86, 12.49) * mm, "end": v(-106, 12.49) * mm});
            skLineSegment(sketch, "E157.0", {"start": v(-182, 12.49) * mm, "end": v(-202, 12.49) * mm});
            skLineSegment(sketch, "E158.bottom", {"start": v(-161.5, -5.51) * mm, "end": v(-126.5, -5.51) * mm});
            skLineSegment(sketch, "E158.top", {"start": v(-161.5, -95.51) * mm, "end": v(-126.5, -95.51) * mm});
            skLineSegment(sketch, "E158.left", {"start": v(-166.5, -10.51) * mm, "end": v(-166.5, -90.51) * mm});
            skLineSegment(sketch, "E158.right", {"start": v(-121.5, -10.51) * mm, "end": v(-121.5, -90.51) * mm});
            skPoint(sketch, "E159.visualSharp", {"position": v(-166.5, -5.51) * mm});
            skArc(sketch, "E159.filletArc", {"start": v(-161.5, -5.51) * mm, "mid": v(-165.04, -6.98) * mm, "end": v(-166.5, -10.51) * mm});
            skPoint(sketch, "E160.visualSharp", {"position": v(-121.5, -5.51) * mm});
            skArc(sketch, "E160.filletArc", {"start": v(-121.5, -10.51) * mm, "mid": v(-122.96, -6.98) * mm, "end": v(-126.5, -5.51) * mm});
            skPoint(sketch, "E161.visualSharp", {"position": v(-121.5, -95.51) * mm});
            skArc(sketch, "E161.filletArc", {"start": v(-126.5, -95.51) * mm, "mid": v(-122.96, -94.05) * mm, "end": v(-121.5, -90.51) * mm});
            skPoint(sketch, "E162.visualSharp", {"position": v(-166.5, -95.51) * mm});
            skArc(sketch, "E162.filletArc", {"start": v(-166.5, -90.51) * mm, "mid": v(-165.04, -94.05) * mm, "end": v(-161.5, -95.51) * mm});
            skSolve(sketch);
        }
        {
            var Q0;
            Q0=makeQuery(id+"F5.imprint","IMPRINT",FACE,{"disambiguationData":[TD([[makeQuery(id+"F5.imprint","IMPRINT",EDGE,{"derivedFrom":sQuery(id+"F5.wireOp",EDGE,"E158.bottom")}),1.0]])]});
            var Q1;
            Q1=makeQuery(id+"F1.opExtrude","SWEPT_FACE",FACE,{"disambiguationData":[OSD([sQuery(id+"F0.wireOp",EDGE,"E0.right")])]});
            extrude(context, id + "F6", {"entities" : qUnion([Q0]), "endBound" : BoundingType.UP_TO_SURFACE, "oppositeDirection" : true, "endBoundEntityFace" : qUnion([Q1]), "depth" : 25 * mm});
        }
        {
            var Q0;
            Q0=makeQuery(id+"F1.opExtrude","SWEPT_FACE",FACE,{"disambiguationData":[OSD([sQuery(id+"F0.wireOp",EDGE,"E0.bottom")])]});
            var sketch = newSketch(context, id + "F7", { "sketchPlane" : qUnion([Q0])});
            skLineSegment(sketch, "E163", {"start": v(-144, 72.09) * mm, "end": v(-144, 34.23) * mm});
            skCircle(sketch, "E164.0", {"center": v(-96, 5.52) * mm, "radius": 10 * mm});
            skCircle(sketch, "E165.0", {"center": v(-192, 5.52) * mm, "radius": 10 * mm});
            skLineSegment(sketch, "E166", {"start": v(-173.1, 75.52) * mm, "end": v(-108.98, 75.52) * mm});
            skLineSegment(sketch, "E167", {"start": v(110.05, 75.52) * mm, "end": v(179.62, 75.52) * mm});
            skLineSegment(sketch, "E168", {"start": v(144, 112.75) * mm, "end": v(144, 0) * mm});
            skSolve(sketch);
        }
        {
            var Q0;
            Q0=qCreatedBy(id+"F4.planeOp",FACE);
            var sketch = newSketch(context, id + "F8", { "sketchPlane" : qUnion([Q0])});
            skLineSegment(sketch, "E169", {"start": v(249.7, 84.35) * mm, "end": v(249.7, 84.93) * mm});
            skLineSegment(sketch, "E170", {"start": v(0, 12.49) * mm, "end": v(292.5, 12.49) * mm});
            skLineSegment(sketch, "E171", {"start": v(292.5, 12.49) * mm, "end": v(292.5, 210.49) * mm});
            skLineSegment(sketch, "E172", {"start": v(292.5, 210.49) * mm, "end": v(246.5, 210.49) * mm});
            skLineSegment(sketch, "E173", {"start": v(246.5, 210.49) * mm, "end": v(221.5, 108.99) * mm});
            skLineSegment(sketch, "E174", {"start": v(221.5, 108.99) * mm, "end": v(0, 41.99) * mm});
            skLineSegment(sketch, "E175", {"start": v(0, 12.49) * mm, "end": v(0, 41.99) * mm});
            skLineSegment(sketch, "E176.0", {"start": v(-10, 12.49) * mm, "end": v(10, 12.49) * mm});
            skLineSegment(sketch, "E177.MirrorCS", {"start": v(-221.5, 108.99) * mm, "end": v(0, 41.99) * mm});
            skLineSegment(sketch, "E178.MirrorCS", {"start": v(0, 12.49) * mm, "end": v(-292.5, 12.49) * mm});
            skLineSegment(sketch, "E179.MirrorCS", {"start": v(-292.5, 12.49) * mm, "end": v(-292.5, 210.49) * mm});
            skLineSegment(sketch, "E180.MirrorCS", {"start": v(-292.5, 210.49) * mm, "end": v(-246.5, 210.49) * mm});
            skLineSegment(sketch, "E181.MirrorCS", {"start": v(-246.5, 210.49) * mm, "end": v(-221.5, 108.99) * mm});
            skLineSegment(sketch, "E182.0", {"start": v(242.38, 210.49) * mm, "end": v(218.16, 112.16) * mm});
            skLineSegment(sketch, "E182.1", {"start": v(218.16, 112.16) * mm, "end": v(0, 46.17) * mm});
            skLineSegment(sketch, "E182.2", {"start": v(-218.16, 112.16) * mm, "end": v(0, 46.17) * mm});
            skLineSegment(sketch, "E182.3", {"start": v(-242.38, 210.49) * mm, "end": v(-218.16, 112.16) * mm});
            skLineSegment(sketch, "E183", {"start": v(-242.38, 210.49) * mm, "end": v(242.38, 210.49) * mm});
            skLineSegment(sketch, "E184", {"start": v(0, 46.17) * mm, "end": v(0, 210.49) * mm});
            skLineSegment(sketch, "E185", {"start": v(242.38, 210.49) * mm, "end": v(246.5, 210.49) * mm});
            skLineSegment(sketch, "E186", {"start": v(-246.5, 210.49) * mm, "end": v(-242.38, 210.49) * mm});
            skSolve(sketch);
        }
        {
            var Q0;
            {var subQ2=sQuery(id+"F5.wireOp",EDGE,"E156.0");Q0=makeQuery(id+"F5.imprint","IMPRINT",FACE,{"disambiguationData":[TD([[makeQuery(id+"F5.imprint","IMPRINT",EDGE,{"derivedFrom":subQ2}),1.0]])]});}
            cPlane(context, id + "F9", {"entities" : qUnion([Q0]), "cplaneType" : CPlaneType.OFFSET, "offset" : 2586 * mm, "oppositeDirection" : true, "width" : 150 * mm, "height" : 150 * mm});
        }
        {
            var Q0;
            Q0=qCreatedBy(id+"F9.planeOp",FACE);
            var sketch = newSketch(context, id + "F10", { "sketchPlane" : qUnion([Q0])});
            skLineSegment(sketch, "E187", {"start": v(0, 46.17) * mm, "end": v(0, 238.17) * mm});
            skLineSegment(sketch, "E188", {"start": v(0, 238.17) * mm, "end": v(271, 238.17) * mm});
            skLineSegment(sketch, "E189", {"start": v(271, 238.17) * mm, "end": v(229.1, 100.17) * mm});
            skLineSegment(sketch, "E190", {"start": v(229.1, 100.17) * mm, "end": v(0, 46.17) * mm});
            skLineSegment(sketch, "E191.MirrorCS", {"start": v(0, 238.17) * mm, "end": v(-271, 238.17) * mm});
            skLineSegment(sketch, "E192.MirrorCS", {"start": v(-271, 238.17) * mm, "end": v(-229.1, 100.17) * mm});
            skLineSegment(sketch, "E193.MirrorCS", {"start": v(-229.1, 100.17) * mm, "end": v(0, 46.17) * mm});
            skLineSegment(sketch, "E194", {"start": v(-271, 238.17) * mm, "end": v(-275.18, 238.17) * mm});
            skLineSegment(sketch, "E195", {"start": v(271, 238.17) * mm, "end": v(275.18, 238.17) * mm});
            skLineSegment(sketch, "E196.0", {"start": v(-275.18, 238.17) * mm, "end": v(-232.25, 96.8) * mm});
            skLineSegment(sketch, "E196.1", {"start": v(-232.25, 96.8) * mm, "end": v(0, 42.06) * mm});
            skLineSegment(sketch, "E196.2", {"start": v(232.25, 96.8) * mm, "end": v(0, 42.06) * mm});
            skLineSegment(sketch, "E196.3", {"start": v(275.18, 238.17) * mm, "end": v(232.25, 96.8) * mm});
            skLineSegment(sketch, "E197.0", {"start": v(-5, 45.7) * mm, "end": v(-5, 7.49) * mm});
            skLineSegment(sketch, "E197.2", {"start": v(10, 7.49) * mm, "end": v(297.5, 7.49) * mm});
            skLineSegment(sketch, "E197.5", {"start": v(-5, 7.49) * mm, "end": v(10, 7.49) * mm});
            skSolve(sketch);
        }
        {
            var Q0;
            {var subQ2=sQuery(id+"F5.wireOp",EDGE,"E156.0");Q0=makeQuery(id+"F5.imprint","IMPRINT",FACE,{"disambiguationData":[TD([[makeQuery(id+"F5.imprint","IMPRINT",EDGE,{"derivedFrom":subQ2}),1.0]])]});}
            cPlane(context, id + "F11", {"entities" : qUnion([Q0]), "cplaneType" : CPlaneType.OFFSET, "offset" : 1961 * mm, "oppositeDirection" : true, "width" : 150 * mm, "height" : 150 * mm});
        }
        {
            var Q0;
            Q0=qCreatedBy(id+"F11.planeOp",FACE);
            var sketch = newSketch(context, id + "F12", { "sketchPlane" : qUnion([Q0])});
            skLineSegment(sketch, "E198.0", {"start": v(176.5, 121.49) * mm, "end": v(0, 56.49) * mm, "construction": true});
            skLineSegment(sketch, "E199.0", {"start": v(-176.5, 121.49) * mm, "end": v(0, 56.49) * mm, "construction": true});
            skLineSegment(sketch, "E200.0", {"start": v(-215, 228.49) * mm, "end": v(-176.5, 121.49) * mm, "construction": true});
            skLineSegment(sketch, "E201.0", {"start": v(215, 228.49) * mm, "end": v(176.5, 121.49) * mm, "construction": true});
            skLineSegment(sketch, "E202.0", {"start": v(210.75, 228.49) * mm, "end": v(173.37, 124.6) * mm, "construction": true});
            skLineSegment(sketch, "E202.1", {"start": v(173.37, 124.6) * mm, "end": v(0, 60.75) * mm, "construction": true});
            skLineSegment(sketch, "E202.2", {"start": v(-173.37, 124.6) * mm, "end": v(0, 60.75) * mm, "construction": true});
            skLineSegment(sketch, "E202.3", {"start": v(-210.75, 228.49) * mm, "end": v(-173.37, 124.6) * mm, "construction": true});
            skLineSegment(sketch, "E203", {"start": v(0, 60.75) * mm, "end": v(0, 273.75) * mm});
            skLineSegment(sketch, "E204", {"start": v(0, 273.75) * mm, "end": v(241, 273.75) * mm});
            skLineSegment(sketch, "E205", {"start": v(241, 273.75) * mm, "end": v(186, 125.75) * mm});
            skLineSegment(sketch, "E206", {"start": v(186, 125.75) * mm, "end": v(0, 60.75) * mm});
            skLineSegment(sketch, "E207", {"start": v(0, 273.75) * mm, "end": v(0, 366.75) * mm});
            skLineSegment(sketch, "E208.MirrorCS", {"start": v(0, 273.75) * mm, "end": v(-241, 273.75) * mm});
            skArc(sketch, "E209", {"start": v(241, 273.75) * mm, "mid": v(0, 366.75) * mm, "end": v(-241, 273.75) * mm});
            skLineSegment(sketch, "E210.MirrorCS", {"start": v(-241, 273.75) * mm, "end": v(-186, 125.75) * mm});
            skLineSegment(sketch, "E211.MirrorCS", {"start": v(-186, 125.75) * mm, "end": v(0, 60.75) * mm});
            skLineSegment(sketch, "E212.0", {"start": v(-245.69, 274.88) * mm, "end": v(-189.1, 122.6) * mm});
            skArc(sketch, "E212.1", {"start": v(245.69, 274.88) * mm, "mid": v(0, 370.75) * mm, "end": v(-245.69, 274.88) * mm});
            skLineSegment(sketch, "E212.2", {"start": v(-189.1, 122.6) * mm, "end": v(0, 56.51) * mm});
            skLineSegment(sketch, "E212.3", {"start": v(189.1, 122.6) * mm, "end": v(0, 56.51) * mm});
            skLineSegment(sketch, "E212.4", {"start": v(245.69, 274.88) * mm, "end": v(189.1, 122.6) * mm});
            skSolve(sketch);
        }
        {
            var Q0;
            {var subQ2=sQuery(id+"F5.wireOp",EDGE,"E156.0");Q0=makeQuery(id+"F5.imprint","IMPRINT",FACE,{"disambiguationData":[TD([[makeQuery(id+"F5.imprint","IMPRINT",EDGE,{"derivedFrom":subQ2}),1.0]])]});}
            cPlane(context, id + "F13", {"entities" : qUnion([Q0]), "cplaneType" : CPlaneType.OFFSET, "offset" : 1946 * mm, "oppositeDirection" : true, "width" : 150 * mm, "height" : 150 * mm});
        }
        {
            var Q0;
            Q0=qCreatedBy(id+"F13.planeOp",FACE);
            var sketch = newSketch(context, id + "F14", { "sketchPlane" : qUnion([Q0])});
            skLineSegment(sketch, "E213.0", {"start": v(-10, 12.49) * mm, "end": v(10, 12.49) * mm});
            skLineSegment(sketch, "E214", {"start": v(0, 12.49) * mm, "end": v(292.5, 12.49) * mm});
            skLineSegment(sketch, "E215", {"start": v(292.5, 12.49) * mm, "end": v(292.5, 160.49) * mm});
            skLineSegment(sketch, "E216", {"start": v(253.5, 228.49) * mm, "end": v(215, 228.49) * mm});
            skLineSegment(sketch, "E217", {"start": v(215, 228.49) * mm, "end": v(176.5, 121.49) * mm});
            skLineSegment(sketch, "E218", {"start": v(176.5, 121.49) * mm, "end": v(0, 56.49) * mm});
            skLineSegment(sketch, "E219", {"start": v(0, 56.49) * mm, "end": v(0, 12.49) * mm});
            skLineSegment(sketch, "E220.MirrorCS", {"start": v(-176.5, 121.49) * mm, "end": v(0, 56.49) * mm});
            skLineSegment(sketch, "E221.MirrorCS", {"start": v(-215, 228.49) * mm, "end": v(-176.5, 121.49) * mm});
            skLineSegment(sketch, "E222.MirrorCS", {"start": v(0, 12.49) * mm, "end": v(-292.5, 12.49) * mm});
            skLineSegment(sketch, "E223.MirrorCS", {"start": v(-292.5, 12.49) * mm, "end": v(-292.5, 160.49) * mm});
            skLineSegment(sketch, "E224.MirrorCS", {"start": v(-253.5, 228.49) * mm, "end": v(-215, 228.49) * mm});
            skLineSegment(sketch, "E225", {"start": v(253.5, 228.49) * mm, "end": v(292.5, 228.49) * mm});
            skLineSegment(sketch, "E226", {"start": v(292.5, 228.49) * mm, "end": v(292.5, 160.49) * mm});
            skLineSegment(sketch, "E227.MirrorCS", {"start": v(-253.5, 228.49) * mm, "end": v(-292.5, 228.49) * mm});
            skLineSegment(sketch, "E228.MirrorCS", {"start": v(-292.5, 228.49) * mm, "end": v(-292.5, 160.49) * mm});
            skLineSegment(sketch, "E229.0", {"start": v(210.75, 228.49) * mm, "end": v(173.37, 124.6) * mm});
            skLineSegment(sketch, "E229.1", {"start": v(173.37, 124.6) * mm, "end": v(0, 60.75) * mm});
            skLineSegment(sketch, "E229.2", {"start": v(-173.37, 124.6) * mm, "end": v(0, 60.75) * mm});
            skLineSegment(sketch, "E229.3", {"start": v(-210.75, 228.49) * mm, "end": v(-173.37, 124.6) * mm});
            skLineSegment(sketch, "E230", {"start": v(-210.75, 228.49) * mm, "end": v(210.75, 228.49) * mm});
            skLineSegment(sketch, "E231", {"start": v(0, 60.75) * mm, "end": v(0, 228.49) * mm});
            skLineSegment(sketch, "E232", {"start": v(-215, 228.49) * mm, "end": v(-210.75, 228.49) * mm});
            skLineSegment(sketch, "E233", {"start": v(210.75, 228.49) * mm, "end": v(215, 228.49) * mm});
            skSolve(sketch);
        }
        {
            var Q0;
            Q0=makeQuery(id+"F1.opExtrude","CAP_FACE",FACE,{"disambiguationData":[OSD([sQuery(id+"F0.wireOp",EDGE,"E0.bottom"),sQuery(id+"F0.wireOp",EDGE,"E0.top"),sQuery(id+"F0.wireOp",EDGE,"E0.left"),sQuery(id+"F0.wireOp",EDGE,"E0.right")])],"isStart":false});
            cPlane(context, id + "F15", {"entities" : qUnion([Q0]), "cplaneType" : CPlaneType.OFFSET, "offset" : 240 * mm, "oppositeDirection" : true, "width" : 150 * mm, "height" : 150 * mm});
        }
        {
            var Q0;
            {var subQ2=sQuery(id+"F5.wireOp",EDGE,"E156.0");Q0=makeQuery(id+"F5.imprint","IMPRINT",FACE,{"disambiguationData":[TD([[makeQuery(id+"F5.imprint","IMPRINT",EDGE,{"derivedFrom":subQ2}),1.0]])]});}
            cPlane(context, id + "F16", {"entities" : qUnion([Q0]), "cplaneType" : CPlaneType.OFFSET, "offset" : 1356 * mm, "oppositeDirection" : true, "width" : 150 * mm, "height" : 150 * mm});
        }
        {
            var Q0;
            {var subQ2=sQuery(id+"F5.wireOp",EDGE,"E156.0");Q0=makeQuery(id+"F5.imprint","IMPRINT",FACE,{"disambiguationData":[TD([[makeQuery(id+"F5.imprint","IMPRINT",EDGE,{"derivedFrom":subQ2}),1.0]])]});}
            cPlane(context, id + "F17", {"entities" : qUnion([Q0]), "cplaneType" : CPlaneType.OFFSET, "offset" : 4016 * mm, "oppositeDirection" : true, "width" : 150 * mm, "height" : 150 * mm});
        }
        {
            var Q0;
            Q0=qCreatedBy(id+"F17.planeOp",FACE);
            var sketch = newSketch(context, id + "F18", { "sketchPlane" : qUnion([Q0])});
            skLineSegment(sketch, "E234.0", {"start": v(-10, 12.49) * mm, "end": v(10, 12.49) * mm});
            skLineSegment(sketch, "E235.0", {"start": v(0, -5.51) * mm, "end": v(0, 12.49) * mm});
            skLineSegment(sketch, "E236", {"start": v(0, 54.49) * mm, "end": v(160.5, 104.49) * mm});
            skLineSegment(sketch, "E237", {"start": v(175.5, 223.49) * mm, "end": v(0, 223.49) * mm});
            skLineSegment(sketch, "E238", {"start": v(0, 223.49) * mm, "end": v(0, 54.49) * mm});
            skLineSegment(sketch, "E239", {"start": v(175.5, 223.49) * mm, "end": v(160.5, 104.49) * mm});
            skLineSegment(sketch, "E240.MirrorCS", {"start": v(-175.5, 223.49) * mm, "end": v(-160.5, 104.49) * mm});
            skLineSegment(sketch, "E241.MirrorCS", {"start": v(-175.5, 223.49) * mm, "end": v(0, 223.49) * mm});
            skLineSegment(sketch, "E242.MirrorCS", {"start": v(0, 54.49) * mm, "end": v(-160.5, 104.49) * mm});
            skLineSegment(sketch, "E243.0", {"start": v(-179.53, 223.49) * mm, "end": v(-164.15, 101.43) * mm});
            skLineSegment(sketch, "E243.1", {"start": v(0, 50.3) * mm, "end": v(-164.15, 101.43) * mm});
            skLineSegment(sketch, "E243.2", {"start": v(0, 50.3) * mm, "end": v(164.15, 101.43) * mm});
            skLineSegment(sketch, "E243.3", {"start": v(179.53, 223.49) * mm, "end": v(164.15, 101.43) * mm});
            skLineSegment(sketch, "E244", {"start": v(175.5, 223.49) * mm, "end": v(179.53, 223.49) * mm});
            skLineSegment(sketch, "E245", {"start": v(-175.5, 223.49) * mm, "end": v(-179.53, 223.49) * mm});
            skSolve(sketch);
        }
        {
            var Q0;
            {var subQ2=sQuery(id+"F5.wireOp",EDGE,"E156.0");Q0=makeQuery(id+"F5.imprint","IMPRINT",FACE,{"disambiguationData":[TD([[makeQuery(id+"F5.imprint","IMPRINT",EDGE,{"derivedFrom":subQ2}),1.0]])]});}
            cPlane(context, id + "F19", {"entities" : qUnion([Q0]), "cplaneType" : CPlaneType.OFFSET, "offset" : 3561 * mm, "oppositeDirection" : true, "width" : 150 * mm, "height" : 150 * mm});
        }
        {
            var Q0;
            Q0=qCreatedBy(id+"F19.planeOp",FACE);
            var sketch = newSketch(context, id + "F20", { "sketchPlane" : qUnion([Q0])});
            skLineSegment(sketch, "E246.0", {"start": v(-10, 12.49) * mm, "end": v(10, 12.49) * mm});
            skLineSegment(sketch, "E247.1", {"start": v(0, -5.51) * mm, "end": v(0, 12.49) * mm});
            skLineSegment(sketch, "E248", {"start": v(225, 244.49) * mm, "end": v(0, 244.49) * mm});
            skLineSegment(sketch, "E249", {"start": v(0, 12.49) * mm, "end": v(4.37, 12.49) * mm});
            skLineSegment(sketch, "E250", {"start": v(192, 102.49) * mm, "end": v(0, 48.49) * mm});
            skLineSegment(sketch, "E251", {"start": v(0, 48.49) * mm, "end": v(0, 244.49) * mm});
            skLineSegment(sketch, "E252", {"start": v(225, 244.49) * mm, "end": v(192, 102.49) * mm});
            skLineSegment(sketch, "E253.MirrorCS", {"start": v(-225, 244.49) * mm, "end": v(0, 244.49) * mm});
            skLineSegment(sketch, "E254.MirrorCS", {"start": v(-225, 244.49) * mm, "end": v(-192, 102.49) * mm});
            skLineSegment(sketch, "E255.MirrorCS", {"start": v(-192, 102.49) * mm, "end": v(0, 48.49) * mm});
            skLineSegment(sketch, "E256.0", {"start": v(-229.1, 244.49) * mm, "end": v(-195.36, 99.28) * mm});
            skLineSegment(sketch, "E256.1", {"start": v(-195.36, 99.28) * mm, "end": v(0, 44.33) * mm});
            skLineSegment(sketch, "E256.2", {"start": v(195.36, 99.28) * mm, "end": v(0, 44.33) * mm});
            skLineSegment(sketch, "E256.3", {"start": v(229.1, 244.49) * mm, "end": v(195.36, 99.28) * mm});
            skLineSegment(sketch, "E257", {"start": v(225, 244.49) * mm, "end": v(229.1, 244.49) * mm});
            skLineSegment(sketch, "E258", {"start": v(-225, 244.49) * mm, "end": v(-229.1, 244.49) * mm});
            skSolve(sketch);
        }
        {
            var Q0;
            Q0=qCreatedBy(id+"F16.planeOp",FACE);
            var sketch = newSketch(context, id + "F21", { "sketchPlane" : qUnion([Q0])});
            skLineSegment(sketch, "E259.0", {"start": v(-10, 12.49) * mm, "end": v(10, 12.49) * mm});
            skLineSegment(sketch, "E260.1", {"start": v(0, -5.51) * mm, "end": v(0, 12.49) * mm});
            skLineSegment(sketch, "E261", {"start": v(0, 92.49) * mm, "end": v(132.5, 170.49) * mm});
            skLineSegment(sketch, "E262", {"start": v(132.5, 170.49) * mm, "end": v(162.5, 278.49) * mm});
            skLineSegment(sketch, "E263", {"start": v(162.5, 278.49) * mm, "end": v(0, 278.49) * mm});
            skLineSegment(sketch, "E264", {"start": v(0, 278.49) * mm, "end": v(0, 92.49) * mm});
            skLineSegment(sketch, "E265.MirrorCS", {"start": v(-162.5, 278.49) * mm, "end": v(0, 278.49) * mm});
            skLineSegment(sketch, "E266.MirrorCS", {"start": v(-132.5, 170.49) * mm, "end": v(-162.5, 278.49) * mm});
            skLineSegment(sketch, "E267.MirrorCS", {"start": v(0, 92.49) * mm, "end": v(-132.5, 170.49) * mm});
            skSolve(sketch);
        }
        {
            var Q0;
            Q0=makeQuery(id+"F21.imprint","IMPRINT",FACE,{"disambiguationData":[TD([[makeQuery(id+"F21.imprint","IMPRINT",EDGE,{"derivedFrom":sQuery(id+"F21.wireOp",EDGE,"E261")}),1.0]])]});
            var Q1;
            Q1=makeQuery(id+"F12.imprint","IMPRINT",FACE,{"disambiguationData":[TD([[makeQuery(id+"F12.imprint","IMPRINT",EDGE,{"derivedFrom":sQuery(id+"F12.wireOp",EDGE,"E203")}),-1.0]])]});
            var Q2;
            Q2=makeQuery(id+"F10.imprint","IMPRINT",FACE,{"disambiguationData":[TD([[makeQuery(id+"F10.imprint","IMPRINT",EDGE,{"derivedFrom":sQuery(id+"F10.wireOp",EDGE,"E187")}),-1.0]])]});
            var Q3;
            Q3=makeQuery(id+"F20.imprint","IMPRINT",FACE,{"disambiguationData":[TD([[makeQuery(id+"F20.imprint","IMPRINT",EDGE,{"derivedFrom":sQuery(id+"F20.wireOp",EDGE,"E248")}),1.0]])]});
            var Q4;
            Q4=makeQuery(id+"F18.imprint","IMPRINT",FACE,{"disambiguationData":[TD([[makeQuery(id+"F18.imprint","IMPRINT",EDGE,{"derivedFrom":sQuery(id+"F18.wireOp",EDGE,"E236")}),1.0]])]});
            loft(context, id + "F22", {"sheetProfilesArray" : [{ "sheetProfileEntities" : qUnion([Q0]) }, { "sheetProfileEntities" : qUnion([Q1]) }, { "sheetProfileEntities" : qUnion([Q2]) }, { "sheetProfileEntities" : qUnion([Q3]) }, { "sheetProfileEntities" : qUnion([Q4]) }]});
        }
    });
